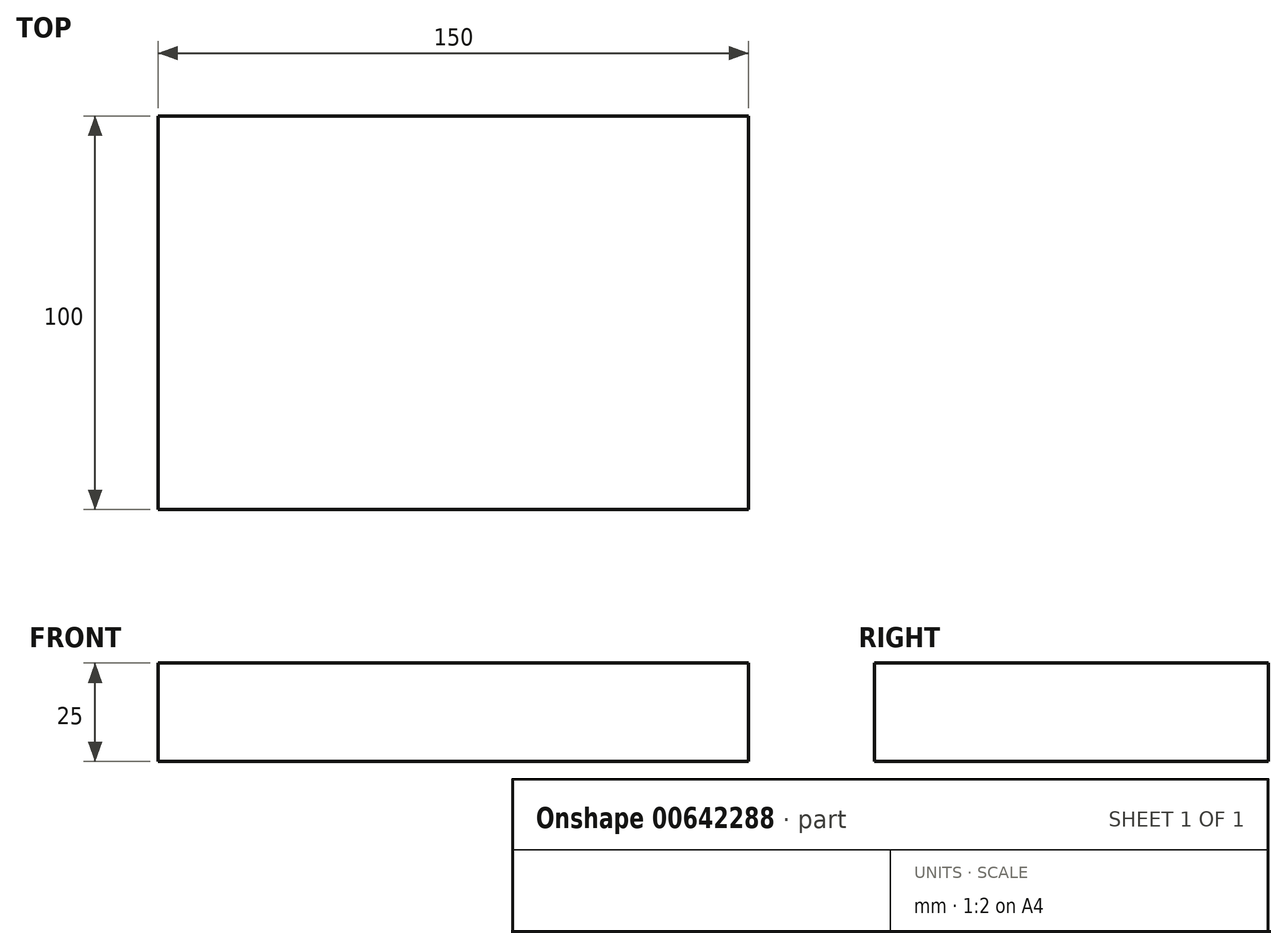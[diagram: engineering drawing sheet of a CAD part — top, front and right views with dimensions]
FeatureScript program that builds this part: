
annotation { "Feature Type Name" : "Feature", "Feature Type Description" : "" }
export const myFeature = defineFeature(function(context is Context, id is Id, definition is map)
    precondition{}
    {
        {
            var Q0;
            Q0=qCreatedBy(makeId("Right.planeOp"),FACE);
            var sketch = newSketch(context, id + "F0", { "sketchPlane" : qUnion([Q0])});
            skLineSegment(sketch, "E0.bottom", {"start": v(50, 12.5) * mm, "end": v(-50, 12.5) * mm});
            skLineSegment(sketch, "E0.top", {"start": v(50, -12.5) * mm, "end": v(-50, -12.5) * mm});
            skLineSegment(sketch, "E0.left", {"start": v(50, 12.5) * mm, "end": v(50, -12.5) * mm});
            skLineSegment(sketch, "E0.right", {"start": v(-50, 12.5) * mm, "end": v(-50, -12.5) * mm});
            skPoint(sketch, "E0.middle", {"position": v(0, 0) * mm});
            skSolve(sketch);
        }
        {
            var Q0;
            Q0=makeQuery(id+"F0.imprint","IMPRINT",FACE,{"disambiguationData":[TD([[makeQuery(id+"F0.imprint","IMPRINT",EDGE,{"derivedFrom":sQuery(id+"F0.wireOp",EDGE,"E0.bottom")}),1.0]])]});
            extrude(context, id + "F1", {"entities" : qUnion([Q0]), "depth" : 150 * mm, "offsetDistance" : 25 * mm});
        }
    });
